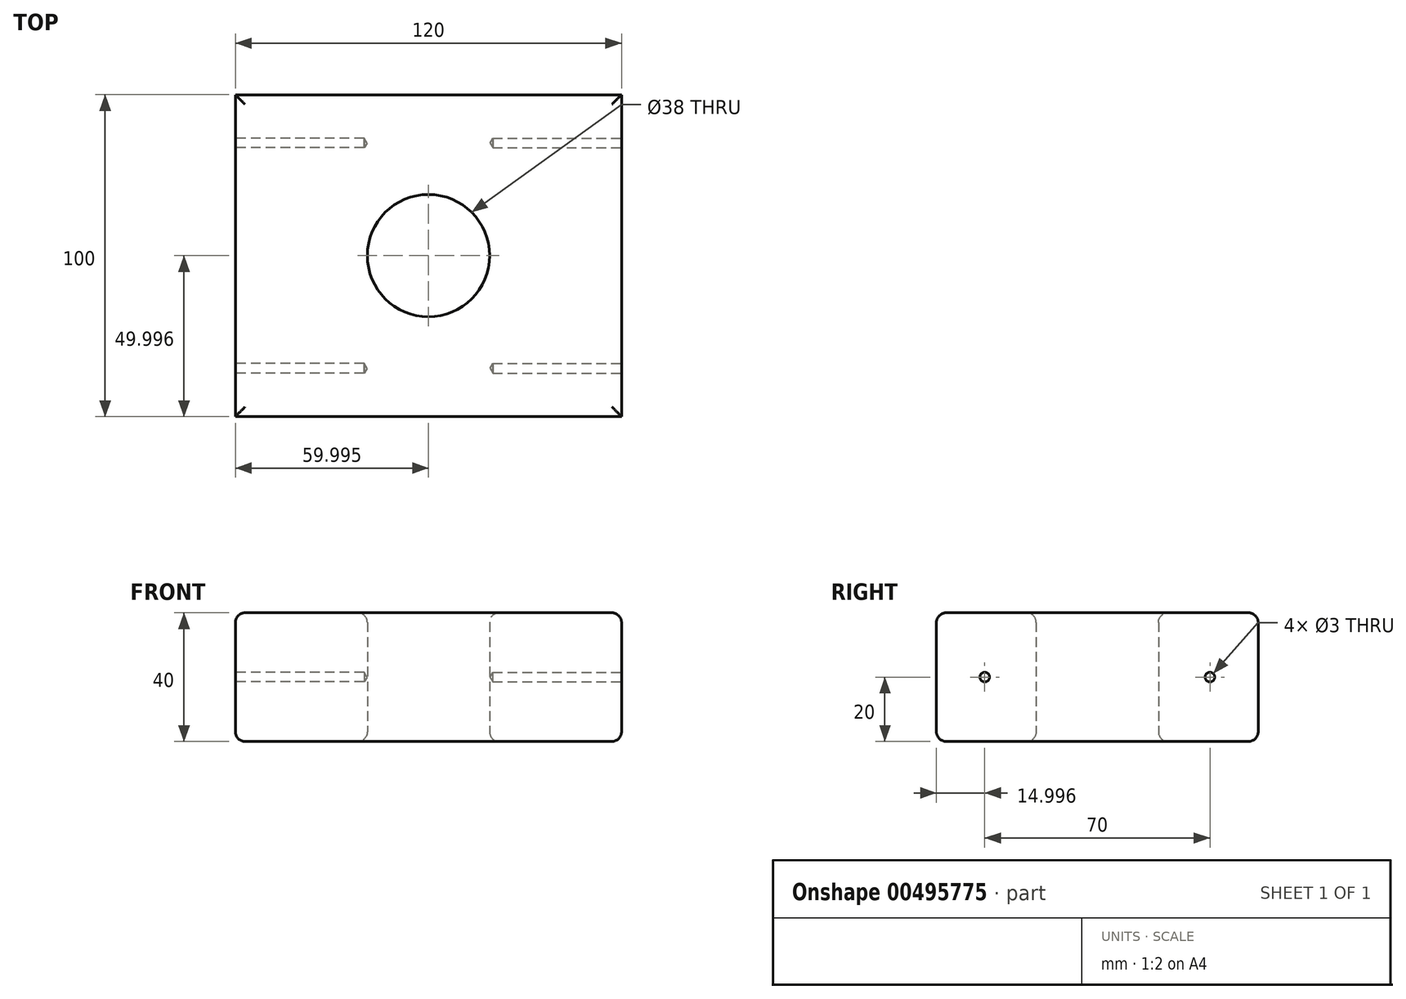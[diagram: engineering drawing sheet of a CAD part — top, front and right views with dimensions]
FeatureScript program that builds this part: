
annotation { "Feature Type Name" : "Feature", "Feature Type Description" : "" }
export const myFeature = defineFeature(function(context is Context, id is Id, definition is map)
    precondition{}
    {
        {
            var Q0;
            Q0=qCreatedBy(makeId("Top.planeOp"),FACE);
            var sketch = newSketch(context, id + "F0", { "sketchPlane" : qUnion([Q0])});
            skLineSegment(sketch, "E0.bottom", {"start": v(-54.66, 75.24) * mm, "end": v(65.34, 75.24) * mm});
            skLineSegment(sketch, "E0.top", {"start": v(-54.66, -24.76) * mm, "end": v(65.34, -24.76) * mm});
            skLineSegment(sketch, "E0.left", {"start": v(-54.66, 75.24) * mm, "end": v(-54.66, 60.24) * mm});
            skLineSegment(sketch, "E0.right", {"start": v(65.34, 75.24) * mm, "end": v(65.34, -24.76) * mm});
            skLineSegment(sketch, "E1", {"start": v(-54.66, 60.24) * mm, "end": v(-54.66, -9.76) * mm});
            skLineSegment(sketch, "E2", {"start": v(-54.66, -9.76) * mm, "end": v(-54.66, -24.76) * mm});
            skPoint(sketch, "E3", {"position": v(-54.66, 25.24) * mm});
            skPoint(sketch, "E4", {"position": v(5.34, 25.24) * mm});
            skCircle(sketch, "E5", {"center": v(5.34, 25.24) * mm, "radius": 19 * mm});
            skPoint(sketch, "E6.orphan", {"position": v(65.34, 25.24) * mm});
            skSolve(sketch);
        }
        {
            var Q0;
            Q0=makeQuery(id+"F0.imprint","IMPRINT",FACE,{"disambiguationData":[TD([[makeQuery(id+"F0.imprint","IMPRINT",EDGE,{"derivedFrom":sQuery(id+"F0.wireOp",EDGE,"E0.bottom")}),-1.0]])]});
            extrude(context, id + "F1", {"entities" : qUnion([Q0]), "endBound" : BoundingType.SYMMETRIC, "depth" : 40 * mm});
        }
        {
            var Q0;
            Q0=makeQuery(id+"F1.opExtrude","CAP_FACE",FACE,{"disambiguationData":[OSD([sQuery(id+"F0.wireOp",EDGE,"E0.bottom"),sQuery(id+"F0.wireOp",EDGE,"E0.top"),sQuery(id+"F0.wireOp",EDGE,"E0.left"),sQuery(id+"F0.wireOp",EDGE,"E0.right"),sQuery(id+"F0.wireOp",EDGE,"E1"),sQuery(id+"F0.wireOp",EDGE,"E2"),sQuery(id+"F0.wireOp",EDGE,"E5")])],"isStart":false});
            var Q1;
            Q1=makeQuery(id+"F1.opExtrude","CAP_EDGE",EDGE,{"disambiguationData":[OSD([sQuery(id+"F0.wireOp",EDGE,"E0.right")])],"isStart":true});
            var Q2;
            Q2=makeQuery(id+"F1.opExtrude","CAP_FACE",FACE,{"disambiguationData":[OSD([sQuery(id+"F0.wireOp",EDGE,"E0.bottom"),sQuery(id+"F0.wireOp",EDGE,"E0.top"),sQuery(id+"F0.wireOp",EDGE,"E0.left"),sQuery(id+"F0.wireOp",EDGE,"E0.right"),sQuery(id+"F0.wireOp",EDGE,"E1"),sQuery(id+"F0.wireOp",EDGE,"E2"),sQuery(id+"F0.wireOp",EDGE,"E5")])],"isStart":true});
            fillet(context, id + "F2", {"entities" : qUnion([Q0, Q1, Q2]), "radius" : 3 * mm, "tangentPropagation" : true, "allowEdgeOverflow" : false});
        }
        {
            var Q0;
            Q0=makeQuery(id+"F1.opExtrude","SWEPT_FACE",FACE,{"disambiguationData":[OSD([sQuery(id+"F0.wireOp",EDGE,"E0.left"),sQuery(id+"F0.wireOp",EDGE,"E1"),sQuery(id+"F0.wireOp",EDGE,"E2")])]});
            var sketch = newSketch(context, id + "F3", { "sketchPlane" : qUnion([Q0])});
            skLineSegment(sketch, "E7", {"start": v(-60.24, 0) * mm, "end": v(9.76, 0) * mm});
            skPoint(sketch, "E8.start.orphan", {"position": v(-75.24, 0) * mm});
            skPoint(sketch, "E9.end.orphan", {"position": v(24.76, 0) * mm});
            skSolve(sketch);
        }
        {
            var Q0;
            Q0=sQuery(id+"F3.wireOp",VERTEX,"E7.end");
            var Q1;
            Q1=sQuery(id+"F3.wireOp",VERTEX,"E7.start");
            var Q2;
            Q2=makeQuery(id+"F1.opExtrude","SWEPT_BODY",BODY,{"disambiguationData":[OSD([sQuery(id+"F0.wireOp",EDGE,"E0.bottom"),sQuery(id+"F0.wireOp",EDGE,"E0.top"),sQuery(id+"F0.wireOp",EDGE,"E0.left"),sQuery(id+"F0.wireOp",EDGE,"E0.right"),sQuery(id+"F0.wireOp",EDGE,"E1"),sQuery(id+"F0.wireOp",EDGE,"E2"),sQuery(id+"F0.wireOp",EDGE,"E5")])]});
            hole(context, id + "F4", {"style" : HoleStyle.SIMPLE, "endStyle" : HoleEndStyle.BLIND, "holeDiameter" : 3 * mm, "holeDepth" : 40 * mm, "isTappedThrough" : true, "tappedDepth" : 12 * mm, "tapClearance" : 3, "locations" : qUnion([Q0, Q1]), "scope" : qUnion([Q2])});
        }
        {
            var Q0;
            Q0=makeQuery(id+"F1.opExtrude","SWEPT_FACE",FACE,{"disambiguationData":[OSD([sQuery(id+"F0.wireOp",EDGE,"E0.right")])]});
            var sketch = newSketch(context, id + "F5", { "sketchPlane" : qUnion([Q0])});
            skPoint(sketch, "E10.endSnap0", {"position": v(75.24, 0) * mm});
            skLineSegment(sketch, "E11", {"start": v(60.24, 0) * mm, "end": v(-9.76, 0) * mm});
            skPoint(sketch, "E10.start.orphan", {"position": v(75.24, 0) * mm});
            skSolve(sketch);
        }
        {
            var Q0;
            Q0=sQuery(id+"F5.wireOp",VERTEX,"E11.start");
            var Q1;
            Q1=sQuery(id+"F5.wireOp",VERTEX,"E11.end");
            var Q2;
            Q2=makeQuery(id+"F1.opExtrude","SWEPT_BODY",BODY,{"disambiguationData":[OSD([sQuery(id+"F0.wireOp",EDGE,"E0.bottom"),sQuery(id+"F0.wireOp",EDGE,"E0.top"),sQuery(id+"F0.wireOp",EDGE,"E0.left"),sQuery(id+"F0.wireOp",EDGE,"E0.right"),sQuery(id+"F0.wireOp",EDGE,"E1"),sQuery(id+"F0.wireOp",EDGE,"E2"),sQuery(id+"F0.wireOp",EDGE,"E5")])]});
            hole(context, id + "F6", {"style" : HoleStyle.SIMPLE, "endStyle" : HoleEndStyle.BLIND, "holeDiameter" : 3 * mm, "holeDepth" : 40 * mm, "isTappedThrough" : true, "tappedDepth" : 12 * mm, "tapClearance" : 3, "locations" : qUnion([Q0, Q1]), "scope" : qUnion([Q2])});
        }
    });
